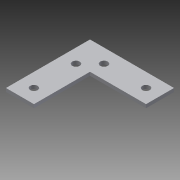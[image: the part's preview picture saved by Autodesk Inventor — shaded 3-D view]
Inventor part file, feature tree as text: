
AUTODESK INVENTOR PART (.ipt)
format: ipt  version: 2014 SP1 (Build 180222100, 222)  size: 108,032 bytes
history: native  units: in
note: dims shown in document units (in); Inventor stores cm internally (conversion verified against a paired STEP export)
features: sketch x2, other x2, sheet_metal_op x1
ambient origin geometry x8: Origin, YZ Plane, XZ Plane, XY Plane, X Axis, Y Axis, Z Axis, Center Point
bodies: Solid1 (feature_tree)
feature tree (5):
  sheet_metal_op  "Face1"
  sketch  "Sketch1"  dims[d1=0.125in]
  other  "Plate1"
  sketch  "Sketch7"  dims[d32=0.615in d44=2.0in d45=0.125in d46=0.0in]
  other  "Cut3"
